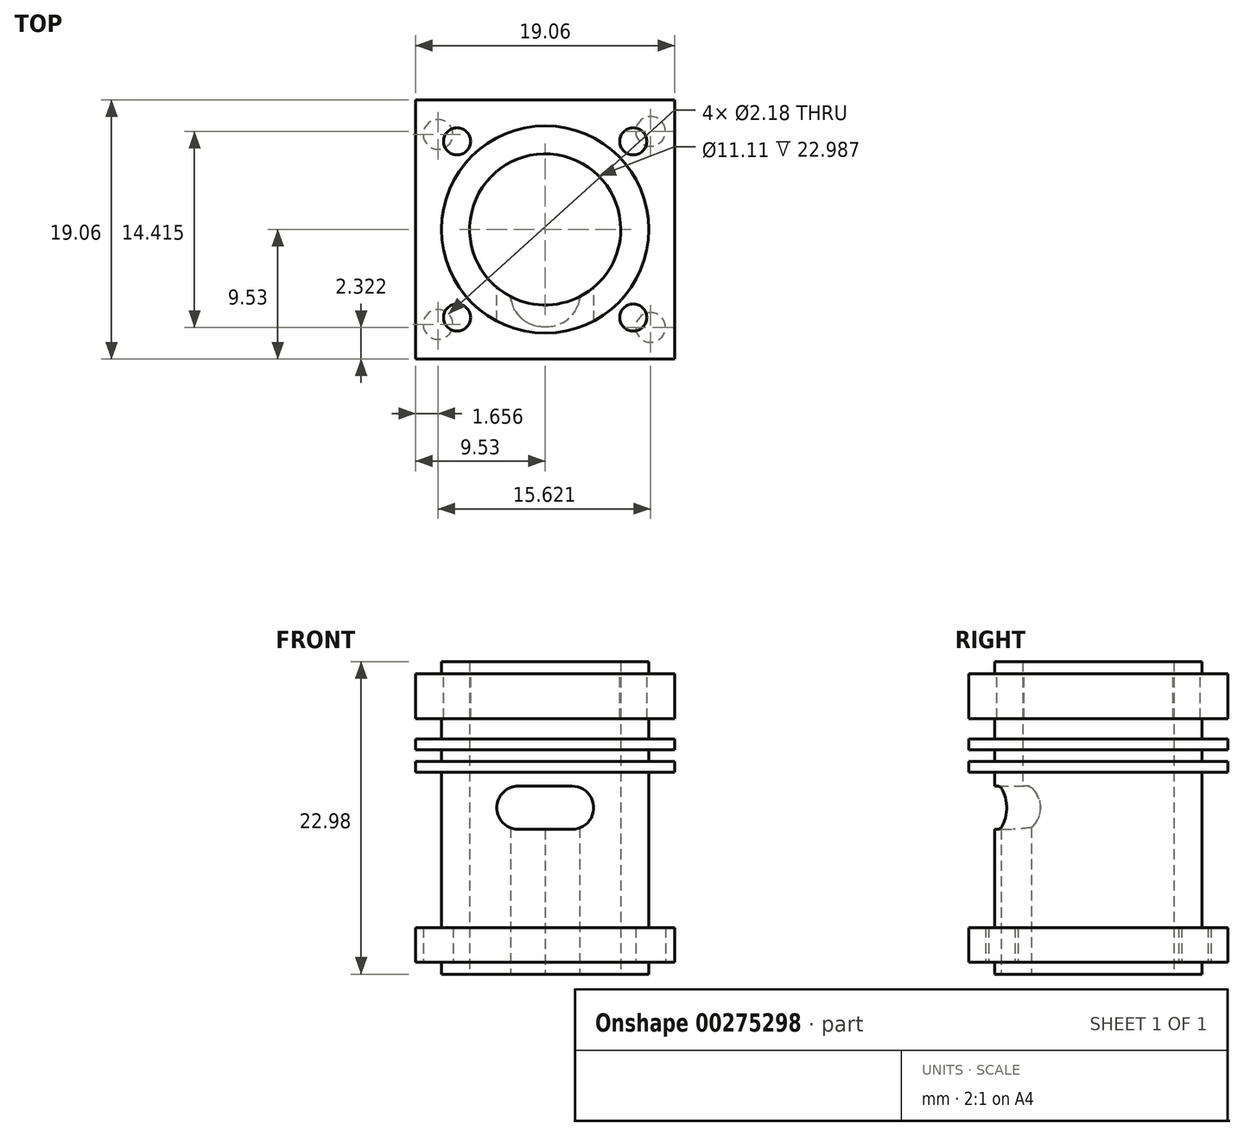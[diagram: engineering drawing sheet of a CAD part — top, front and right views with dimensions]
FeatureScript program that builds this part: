
annotation { "Feature Type Name" : "Feature", "Feature Type Description" : "" }
export const myFeature = defineFeature(function(context is Context, id is Id, definition is map)
    precondition{}
    {
        {
            var Q0;
            Q0=qCreatedBy(makeId("Top.planeOp"),FACE);
            var sketch = newSketch(context, id + "F0", { "sketchPlane" : qUnion([Q0])});
            skCircle(sketch, "E0", {"center": v(0, 0) * mm, "radius": 7.62 * mm});
            skCircle(sketch, "E1", {"center": v(0, 0) * mm, "radius": 5.56 * mm});
            skSolve(sketch);
        }
        {
            var Q0;
            Q0 = qSketchRegion(id + "F0", true);
            extrude(context, id + "F1", {"entities" : qUnion([Q0]), "endBound" : BoundingType.SYMMETRIC, "depth" : 22.99 * mm});
        }
        {
            var Q0;
            Q0=makeQuery(id+"F1.opExtrude","CAP_FACE",FACE,{"disambiguationData":[OSD([sQuery(id+"F0.wireOp",EDGE,"E0"),sQuery(id+"F0.wireOp",EDGE,"E1")])],"isStart":true});
            cPlane(context, id + "F2", {"entities" : qUnion([Q0]), "cplaneType" : CPlaneType.OFFSET, "offset" : 0.89 * mm, "oppositeDirection" : true, "width" : 152.4 * mm, "height" : 152.4 * mm});
        }
        {
            var Q0;
            Q0=qCreatedBy(id+"F2.planeOp",FACE);
            var sketch = newSketch(context, id + "F3", { "sketchPlane" : qUnion([Q0])});
            skLineSegment(sketch, "E2.bottom", {"start": v(9.52, 9.52) * mm, "end": v(-9.53, 9.52) * mm});
            skLineSegment(sketch, "E2.top", {"start": v(9.52, -9.53) * mm, "end": v(-9.53, -9.53) * mm});
            skLineSegment(sketch, "E2.left", {"start": v(9.53, 9.52) * mm, "end": v(9.52, -9.53) * mm});
            skLineSegment(sketch, "E2.right", {"start": v(-9.53, 9.52) * mm, "end": v(-9.53, -9.53) * mm});
            skPoint(sketch, "E2.middle", {"position": v(0, 0) * mm});
            skCircle(sketch, "E3.0", {"center": v(0, 0) * mm, "radius": 5.56 * mm});
            skSolve(sketch);
        }
        {
            var Q0;
            Q0 = qSketchRegion(id + "F3", true);
            extrude(context, id + "F4", {"entities" : qUnion([Q0]), "operationType" : NewBodyOperationType.ADD, "oppositeDirection" : true, "depth" : 2.54 * mm});
        }
        {
            var Q0;
            Q0=makeQuery(id+"F4.opExtrude","CAP_FACE",FACE,{"disambiguationData":[OSD([sQuery(id+"F3.wireOp",EDGE,"E2.bottom"),sQuery(id+"F3.wireOp",EDGE,"E2.top"),sQuery(id+"F3.wireOp",EDGE,"E2.left"),sQuery(id+"F3.wireOp",EDGE,"E2.right"),sQuery(id+"F3.wireOp",EDGE,"E3.0")])],"isStart":true});
            cPlane(context, id + "F5", {"entities" : qUnion([Q0]), "cplaneType" : CPlaneType.OFFSET, "offset" : 13.97 * mm, "oppositeDirection" : true, "width" : 152.4 * mm, "height" : 152.4 * mm});
        }
        {
            var Q0;
            Q0=qCreatedBy(id+"F5.planeOp",FACE);
            var sketch = newSketch(context, id + "F6", { "sketchPlane" : qUnion([Q0])});
            skLineSegment(sketch, "E4.0", {"start": v(-9.53, 9.52) * mm, "end": v(-9.53, -9.53) * mm});
            skLineSegment(sketch, "E5.0", {"start": v(9.52, -9.53) * mm, "end": v(-9.53, -9.53) * mm});
            skLineSegment(sketch, "E6.0", {"start": v(9.53, 9.52) * mm, "end": v(9.52, -9.53) * mm});
            skLineSegment(sketch, "E7.0", {"start": v(9.52, 9.52) * mm, "end": v(-9.53, 9.52) * mm});
            skCircle(sketch, "E8.0", {"center": v(0, 0) * mm, "radius": 5.56 * mm});
            skSolve(sketch);
        }
        {
            var Q0;
            Q0 = qSketchRegion(id + "F6", true);
            extrude(context, id + "F7", {"entities" : qUnion([Q0]), "operationType" : NewBodyOperationType.ADD, "oppositeDirection" : true, "depth" : 0.8 * mm});
        }
        {
            var Q0;
            Q0=makeQuery(id+"F1.opExtrude","CAP_FACE",FACE,{"disambiguationData":[OSD([sQuery(id+"F0.wireOp",EDGE,"E0"),sQuery(id+"F0.wireOp",EDGE,"E1")])],"isStart":true});
            cPlane(context, id + "F8", {"entities" : qUnion([Q0]), "cplaneType" : CPlaneType.OFFSET, "offset" : 16.5 * mm, "oppositeDirection" : true, "width" : 152.4 * mm, "height" : 152.4 * mm});
        }
        {
            var Q0;
            Q0=qCreatedBy(id+"F8.planeOp",FACE);
            var sketch = newSketch(context, id + "F9", { "sketchPlane" : qUnion([Q0])});
            skLineSegment(sketch, "E9.0", {"start": v(9.52, 9.52) * mm, "end": v(-9.53, 9.52) * mm});
            skLineSegment(sketch, "E10.0", {"start": v(-9.53, 9.52) * mm, "end": v(-9.53, -9.53) * mm});
            skLineSegment(sketch, "E11.0", {"start": v(9.52, -9.53) * mm, "end": v(-9.53, -9.53) * mm});
            skLineSegment(sketch, "E12.0", {"start": v(9.53, 9.52) * mm, "end": v(9.52, -9.53) * mm});
            skCircle(sketch, "E13.0", {"center": v(0, 0) * mm, "radius": 5.56 * mm});
            skSolve(sketch);
        }
        {
            var Q0;
            Q0 = qSketchRegion(id + "F9", true);
            extrude(context, id + "F10", {"entities" : qUnion([Q0]), "operationType" : NewBodyOperationType.ADD, "oppositeDirection" : true, "depth" : 0.8 * mm});
        }
        {
            var Q0;
            Q0=makeQuery(id+"F1.opExtrude","CAP_FACE",FACE,{"disambiguationData":[OSD([sQuery(id+"F0.wireOp",EDGE,"E0"),sQuery(id+"F0.wireOp",EDGE,"E1")])],"isStart":true});
            cPlane(context, id + "F11", {"entities" : qUnion([Q0]), "cplaneType" : CPlaneType.OFFSET, "offset" : 18.8 * mm, "oppositeDirection" : true, "width" : 152.4 * mm, "height" : 152.4 * mm});
        }
        {
            var Q0;
            Q0=qCreatedBy(id+"F11.planeOp",FACE);
            var sketch = newSketch(context, id + "F12", { "sketchPlane" : qUnion([Q0])});
            skLineSegment(sketch, "E14.0", {"start": v(-9.53, 9.52) * mm, "end": v(-9.53, -9.53) * mm});
            skLineSegment(sketch, "E15.0", {"start": v(9.52, -9.53) * mm, "end": v(-9.53, -9.53) * mm});
            skLineSegment(sketch, "E16.0", {"start": v(9.53, 9.52) * mm, "end": v(9.52, -9.53) * mm});
            skLineSegment(sketch, "E17.0", {"start": v(9.52, 9.52) * mm, "end": v(-9.53, 9.52) * mm});
            skCircle(sketch, "E18.0", {"center": v(0, 0) * mm, "radius": 5.56 * mm});
            skSolve(sketch);
        }
        {
            var Q0;
            Q0 = qSketchRegion(id + "F12", true);
            extrude(context, id + "F13", {"entities" : qUnion([Q0]), "operationType" : NewBodyOperationType.ADD, "oppositeDirection" : true, "depth" : 3.3 * mm});
        }
        {
            var Q0;
            Q0=makeQuery(id+"F13.opExtrude","CAP_FACE",FACE,{"disambiguationData":[OSD([sQuery(id+"F12.wireOp",EDGE,"E14.0"),sQuery(id+"F12.wireOp",EDGE,"E15.0"),sQuery(id+"F12.wireOp",EDGE,"E16.0"),sQuery(id+"F12.wireOp",EDGE,"E17.0"),sQuery(id+"F12.wireOp",EDGE,"E18.0")])],"isStart":false});
            var sketch = newSketch(context, id + "F14", { "sketchPlane" : qUnion([Q0])});
            skPoint(sketch, "E19", {"position": v(-6.48, 6.48) * mm});
            skPoint(sketch, "E20", {"position": v(6.48, 6.48) * mm});
            skPoint(sketch, "E21", {"position": v(6.48, -6.48) * mm});
            skPoint(sketch, "E22", {"position": v(-6.48, -6.48) * mm});
            skSolve(sketch);
        }
        {
            var Q0;
            Q0=sQuery(id+"F14.wireOp",VERTEX,"E22");
            var Q1;
            Q1=sQuery(id+"F14.wireOp",VERTEX,"E19");
            var Q2;
            Q2=sQuery(id+"F14.wireOp",VERTEX,"E20");
            var Q3;
            Q3=sQuery(id+"F14.wireOp",VERTEX,"E21");
            var Q4;
            Q4=makeQuery(id+"F1.opExtrude","SWEPT_BODY",BODY,{"disambiguationData":[OSD([sQuery(id+"F0.wireOp",EDGE,"E0"),sQuery(id+"F0.wireOp",EDGE,"E1")])]});
            hole(context, id + "F15", {"style" : HoleStyle.SIMPLE, "endStyle" : HoleEndStyle.BLIND, "holeDiameter" : 2 * mm, "holeDepth" : 3.3 * mm, "tappedDepth" : 12.7 * mm, "tapClearance" : 3, "locations" : qUnion([Q0, Q1, Q2, Q3]), "scope" : qUnion([Q4])});
        }
        {
            var Q0;
            Q0=makeQuery(id+"F4.opExtrude","CAP_FACE",FACE,{"disambiguationData":[OSD([sQuery(id+"F3.wireOp",EDGE,"E2.bottom"),sQuery(id+"F3.wireOp",EDGE,"E2.top"),sQuery(id+"F3.wireOp",EDGE,"E2.left"),sQuery(id+"F3.wireOp",EDGE,"E2.right"),sQuery(id+"F3.wireOp",EDGE,"E3.0")])],"isStart":true});
            var sketch = newSketch(context, id + "F16", { "sketchPlane" : qUnion([Q0])});
            skCircle(sketch, "E23", {"center": v(-7.87, 6.99) * mm, "radius": 1.1 * mm});
            skCircle(sketch, "E24", {"center": v(7.75, 7.2) * mm, "radius": 1.1 * mm});
            skCircle(sketch, "E25", {"center": v(7.75, -7.2) * mm, "radius": 1.1 * mm});
            skCircle(sketch, "E26", {"center": v(-7.87, -6.99) * mm, "radius": 1.1 * mm});
            skSolve(sketch);
        }
        {
            var Q0;
            Q0 = qSketchRegion(id + "F16", true);
            var Q1;
            Q1=makeQuery(id+"F4.opExtrude","CAP_FACE",FACE,{"disambiguationData":[OSD([sQuery(id+"F3.wireOp",EDGE,"E2.bottom"),sQuery(id+"F3.wireOp",EDGE,"E2.top"),sQuery(id+"F3.wireOp",EDGE,"E2.left"),sQuery(id+"F3.wireOp",EDGE,"E2.right"),sQuery(id+"F3.wireOp",EDGE,"E3.0")])],"isStart":false});
            extrude(context, id + "F17", {"entities" : qUnion([Q0]), "operationType" : NewBodyOperationType.REMOVE, "endBound" : BoundingType.UP_TO_SURFACE, "oppositeDirection" : true, "endBoundEntityFace" : qUnion([Q1]), "depth" : 25.4 * mm});
        }
        {
            var Q0;
            Q0=makeQuery(id+"F1.opExtrude","CAP_FACE",FACE,{"disambiguationData":[OSD([sQuery(id+"F0.wireOp",EDGE,"E0"),sQuery(id+"F0.wireOp",EDGE,"E1")])],"isStart":true});
            var sketch = newSketch(context, id + "F18", { "sketchPlane" : qUnion([Q0])});
            skLineSegment(sketch, "E27.0", {"start": v(9.52, 9.52) * mm, "end": v(-9.53, 9.52) * mm, "construction": true});
            skLineSegment(sketch, "E28.0", {"start": v(9.52, -9.53) * mm, "end": v(-9.53, -9.53) * mm, "construction": true});
            skLineSegment(sketch, "E29", {"start": v(0, 9.52) * mm, "end": v(0, -9.53) * mm, "construction": true});
            skArc(sketch, "E30", {"start": v(0, 7.13) * mm, "mid": v(-1.72, 6.56) * mm, "end": v(-2.55, 4.94) * mm});
            skArc(sketch, "E31", {"start": v(2.55, 4.94) * mm, "mid": v(1.72, 6.56) * mm, "end": v(0, 7.13) * mm});
            skArc(sketch, "E32.0", {"start": v(2.55, 4.94) * mm, "mid": v(0, 5.56) * mm, "end": v(-2.55, 4.94) * mm});
            skSolve(sketch);
        }
        {
            var Q0;
            Q0 = qSketchRegion(id + "F18", true);
            extrude(context, id + "F19", {"entities" : qUnion([Q0]), "operationType" : NewBodyOperationType.REMOVE, "oppositeDirection" : true, "depth" : 11.43 * mm});
        }
        {
            var Q0;
            Q0=qCreatedBy(makeId("Front.planeOp"),FACE);
            var sketch = newSketch(context, id + "F20", { "sketchPlane" : qUnion([Q0])});
            skLineSegment(sketch, "E33", {"start": v(5.56, 11.5) * mm, "end": v(5.56, -11.5) * mm, "construction": true});
            skLineSegment(sketch, "E34", {"start": v(-5.56, -11.5) * mm, "end": v(-5.56, 11.5) * mm, "construction": true});
            skLineSegment(sketch, "E35.0", {"start": v(-5.56, 11.5) * mm, "end": v(5.56, 11.5) * mm, "construction": true});
            skLineSegment(sketch, "E36.0", {"start": v(-5.56, -11.5) * mm, "end": v(5.56, -11.5) * mm, "construction": true});
            skLineSegment(sketch, "E37", {"start": v(0, 11.5) * mm, "end": v(0, -11.5) * mm, "construction": true});
            skArc(sketch, "E38", {"start": v(-1.98, 2.34) * mm, "mid": v(-3.57, 0.75) * mm, "end": v(-1.98, -0.84) * mm});
            skArc(sketch, "E39", {"start": v(1.98, -0.84) * mm, "mid": v(3.57, 0.75) * mm, "end": v(1.98, 2.34) * mm});
            skLineSegment(sketch, "E40", {"start": v(-1.98, 2.34) * mm, "end": v(1.98, 2.34) * mm});
            skLineSegment(sketch, "E41", {"start": v(-1.98, -0.84) * mm, "end": v(1.98, -0.84) * mm});
            skLineSegment(sketch, "E42.0", {"start": v(-7.62, -11.5) * mm, "end": v(7.62, -11.5) * mm, "construction": true});
            skSolve(sketch);
        }
        {
            var Q0;
            Q0 = qSketchRegion(id + "F20", true);
            extrude(context, id + "F21", {"entities" : qUnion([Q0]), "operationType" : NewBodyOperationType.REMOVE, "depth" : 11.43 * mm});
        }
    });
